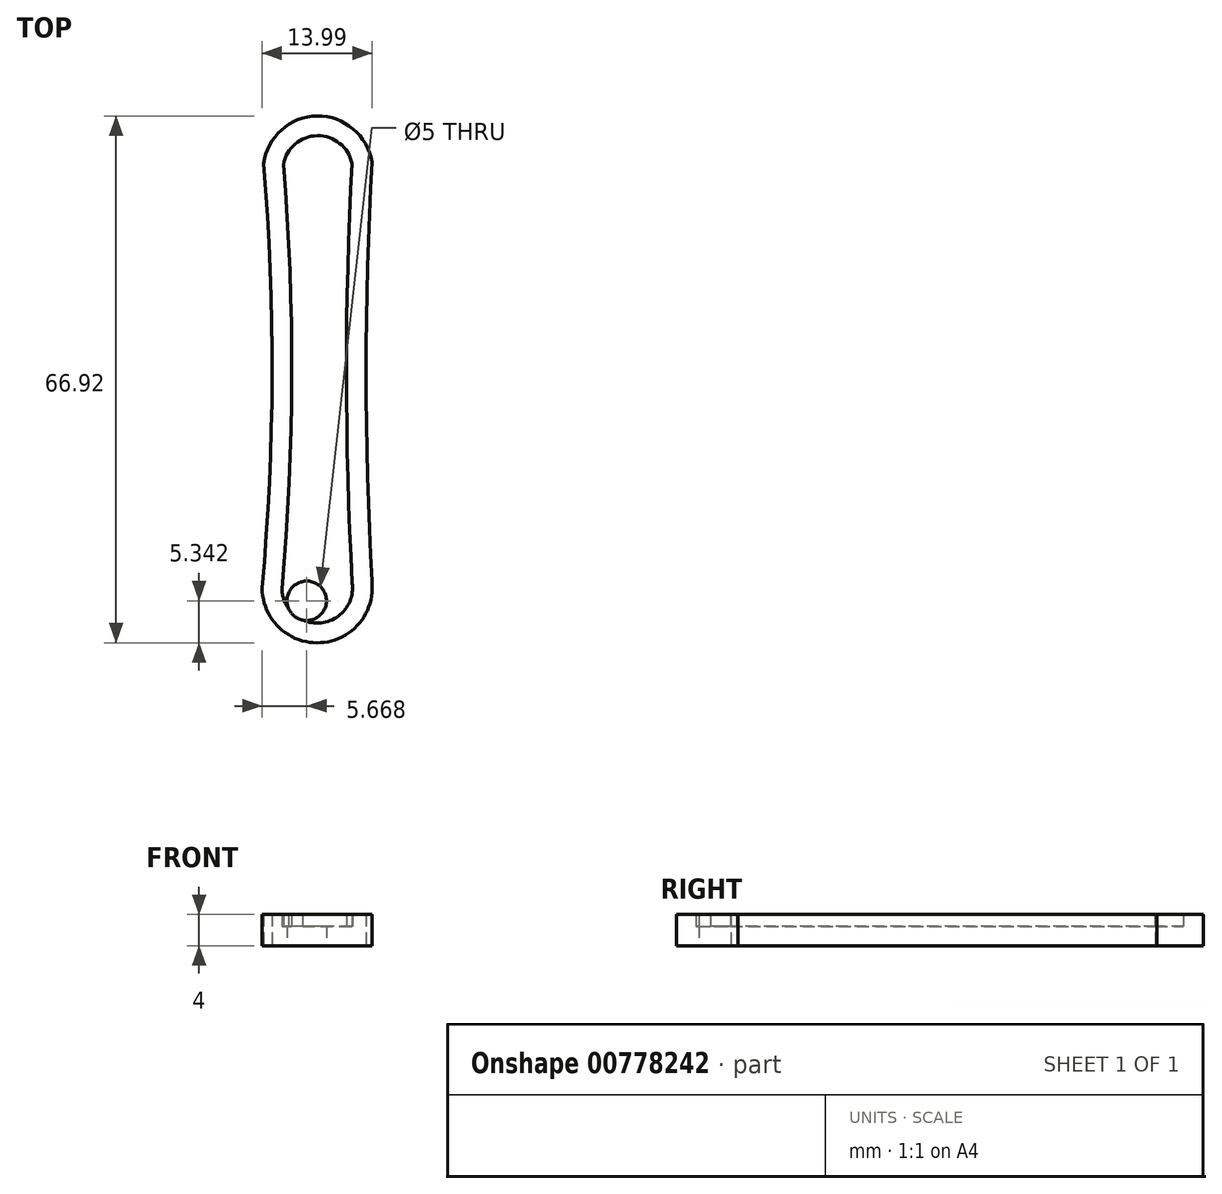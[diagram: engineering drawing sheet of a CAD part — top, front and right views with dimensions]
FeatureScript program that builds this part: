
annotation { "Feature Type Name" : "Feature", "Feature Type Description" : "" }
export const myFeature = defineFeature(function(context is Context, id is Id, definition is map)
    precondition{}
    {
        {
            var Q0;
            Q0=qCreatedBy(makeId("Top.planeOp"),FACE);
            var sketch = newSketch(context, id + "F0", { "sketchPlane" : qUnion([Q0])});
            skArc(sketch, "E0", {"start": v(-29.37, 65.5) * mm, "mid": v(-36.33, 71.37) * mm, "end": v(-43.11, 65.3) * mm});
            skArc(sketch, "E1", {"start": v(-43.3, 11.4) * mm, "mid": v(-35.87, 4.46) * mm, "end": v(-29.37, 12.28) * mm});
            skArc(sketch, "E2", {"start": v(-43.3, 11.4) * mm, "mid": v(-42.04, 38.35) * mm, "end": v(-43.11, 65.3) * mm});
            skArc(sketch, "E3", {"start": v(-29.37, 65.5) * mm, "mid": v(-30.1, 38.9) * mm, "end": v(-29.37, 12.28) * mm});
            skSolve(sketch);
        }
        {
            var Q0;
            Q0 = qSketchRegion(id + "F0", true);
            extrude(context, id + "F1", {"entities" : qUnion([Q0]), "depth" : 4 * mm, "offsetDistance" : 25 * mm});
        }
        {
            var Q0;
            Q0=qCreatedBy(makeId("Top.planeOp"),FACE);
            var sketch = newSketch(context, id + "F2", { "sketchPlane" : qUnion([Q0])});
            skCircle(sketch, "E4", {"center": v(-38.07, 64.37) * mm, "radius": 1.73 * mm});
            skSolve(sketch);
        }
        {
            var Q0;
            Q0=makeQuery(id+"F1.opExtrude","CAP_FACE",FACE,{"disambiguationData":[OSD([sQuery(id+"F0.wireOp",EDGE,"E0"),sQuery(id+"F0.wireOp",EDGE,"E1"),sQuery(id+"F0.wireOp",EDGE,"E2"),sQuery(id+"F0.wireOp",EDGE,"E3")])],"isStart":false});
            shell(context, id + "F3", {"entities" : qUnion([Q0]), "thickness" : 2.5 * mm});
        }
        {
            var Q0;
            Q0 = qSketchRegion(id + "F2", true);
            extrude(context, id + "F4", {"entities" : qUnion([Q0]), "operationType" : NewBodyOperationType.REMOVE, "oppositeDirection" : true, "depth" : 25 * mm, "offsetDistance" : 25 * mm});
        }
        {
            var Q0;
            Q0=makeQuery(id+"F1.opExtrude","CAP_FACE",FACE,{"disambiguationData":[OSD([sQuery(id+"F0.wireOp",EDGE,"E0"),sQuery(id+"F0.wireOp",EDGE,"E1"),sQuery(id+"F0.wireOp",EDGE,"E2"),sQuery(id+"F0.wireOp",EDGE,"E3")])],"isStart":true});
            var sketch = newSketch(context, id + "F5", { "sketchPlane" : qUnion([Q0])});
            skCircle(sketch, "E5", {"center": v(-37.64, -9.8) * mm, "radius": 2.33 * mm});
            skSolve(sketch);
        }
        {
            var Q0;
            Q0=sQuery(id+"F5.wireOp",VERTEX,"E5.center");
            var Q1;
            Q1=makeQuery(id+"F1.opExtrude","SWEPT_BODY",BODY,{"disambiguationData":[OSD([sQuery(id+"F0.wireOp",EDGE,"E0"),sQuery(id+"F0.wireOp",EDGE,"E1"),sQuery(id+"F0.wireOp",EDGE,"E2"),sQuery(id+"F0.wireOp",EDGE,"E3")])]});
            hole(context, id + "F6", {"style" : HoleStyle.SIMPLE, "endStyle" : HoleEndStyle.THROUGH, "holeDiameter" : 5 * mm, "majorDiameter" : 5 * mm, "isTappedThrough" : true, "tappedDepth" : 12 * mm, "tapClearance" : 3, "locations" : qUnion([Q0]), "scope" : qUnion([Q1])});
        }
    });
